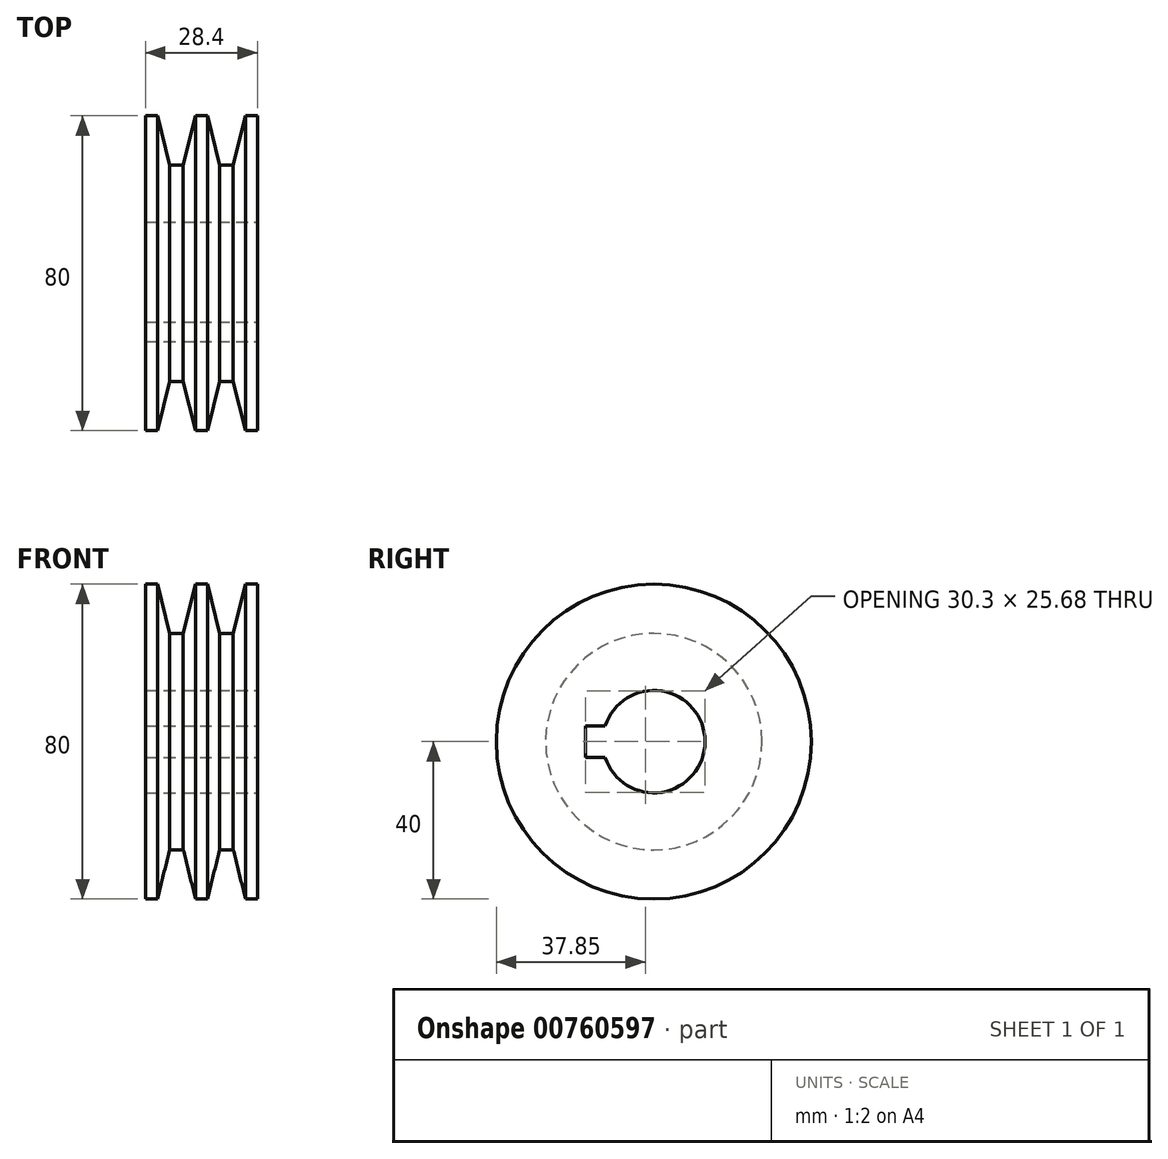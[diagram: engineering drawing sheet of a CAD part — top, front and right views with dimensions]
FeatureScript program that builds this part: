
annotation { "Feature Type Name" : "Feature", "Feature Type Description" : "" }
export const myFeature = defineFeature(function(context is Context, id is Id, definition is map)
    precondition{}
    {
        {
            var Q0;
            Q0=qCreatedBy(makeId("Right.planeOp"),FACE);
            var sketch = newSketch(context, id + "F0", { "sketchPlane" : qUnion([Q0])});
            skArc(sketch, "E0", {"start": v(-12.37, -4) * mm, "mid": v(13, 0) * mm, "end": v(-12.37, 4) * mm});
            skLineSegment(sketch, "E1.bottom", {"start": v(-17.3, -4) * mm, "end": v(-12.37, -4) * mm});
            skLineSegment(sketch, "E1.top", {"start": v(-17.3, 4) * mm, "end": v(-12.37, 4) * mm});
            skLineSegment(sketch, "E1.left", {"start": v(-17.3, -4) * mm, "end": v(-17.3, 4) * mm});
            skLineSegment(sketch, "E2", {"start": v(-17.3, 0) * mm, "end": v(0, 0) * mm, "construction": true});
            skSolve(sketch);
        }
        {
            var Q0;
            Q0=qCreatedBy(makeId("Front.planeOp"),FACE);
            var sketch = newSketch(context, id + "F1", { "sketchPlane" : qUnion([Q0])});
            skLineSegment(sketch, "E3", {"start": v(-14.2, 0) * mm, "end": v(-14.2, 40) * mm});
            skLineSegment(sketch, "E4", {"start": v(-14.2, 40) * mm, "end": v(-11.2, 40) * mm});
            skLineSegment(sketch, "E5", {"start": v(-11.2, 40) * mm, "end": v(-8.08, 27.5) * mm});
            skLineSegment(sketch, "E6", {"start": v(-8.08, 27.5) * mm, "end": v(-4.62, 27.5) * mm});
            skLineSegment(sketch, "E7", {"start": v(-4.62, 27.5) * mm, "end": v(-1.5, 40) * mm});
            skLineSegment(sketch, "E8", {"start": v(-1.5, 40) * mm, "end": v(1.5, 40) * mm});
            skLineSegment(sketch, "E9", {"start": v(1.5, 40) * mm, "end": v(4.62, 27.5) * mm});
            skLineSegment(sketch, "E10", {"start": v(4.62, 27.5) * mm, "end": v(8.08, 27.5) * mm});
            skLineSegment(sketch, "E11", {"start": v(8.08, 27.5) * mm, "end": v(11.2, 40) * mm});
            skLineSegment(sketch, "E12", {"start": v(11.2, 40) * mm, "end": v(14.2, 40) * mm});
            skLineSegment(sketch, "E13", {"start": v(14.2, 40) * mm, "end": v(14.2, 0) * mm});
            skLineSegment(sketch, "E14", {"start": v(14.2, 0) * mm, "end": v(-14.2, 0) * mm});
            skSolve(sketch);
        }
        {
            var Q0;
            Q0 = qSketchRegion(id + "F1", true);
            var Q1;
            Q1=sQuery(id+"F1.wireOp",EDGE,"E14");
            revolve(context, id + "F2", {"surfaceOperationType" : NewSurfaceOperationType.NEW, "entities" : qUnion([Q0]), "axis" : qUnion([Q1]), "revolveType" : RevolveType.FULL});
        }
        {
            var Q0;
            Q0 = qSketchRegion(id + "F0", true);
            extrude(context, id + "F3", {"entities" : qUnion([Q0]), "operationType" : NewBodyOperationType.REMOVE, "endBound" : BoundingType.SYMMETRIC, "oppositeDirection" : true, "depth" : 28.4 * mm, "offsetDistance" : 25 * mm});
        }
    });
